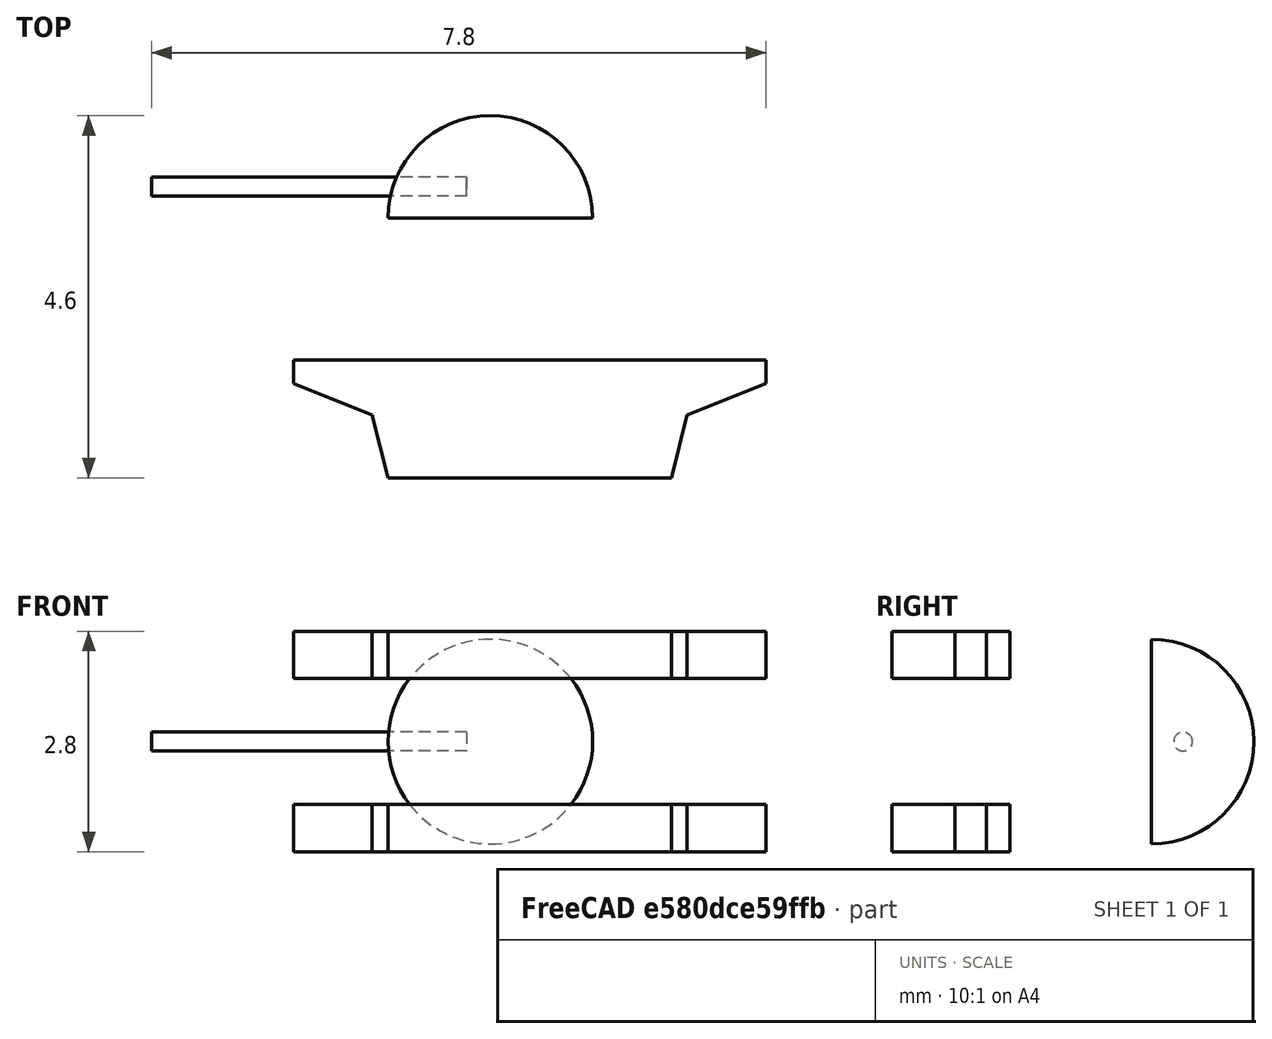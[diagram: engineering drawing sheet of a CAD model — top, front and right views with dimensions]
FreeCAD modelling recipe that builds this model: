
FCSTD DOCUMENT  (FreeCAD 0.15R4671 (Git))
Label: track
License: All rights reserved
LicenseURL: http://en.wikipedia.org/wiki/All_rights_reserved
objects: Part::Part2DObjectPython×2, Part::Extrusion×2, Mesh::Feature×1, Part::Sphere×1, Part::Cylinder×1
note: 6 computed .brp shape members not serialized (recipe doc carries the construction recipe); baked Part::Feature solids carry a one-line shape summary decoded from their .brp

FEATURE [Part::Part2DObjectPython] DWire  # Draft 2D object (typed FeaturePython)
  ChamferSize = 0
  Closed = true
  End = (3,1.2,0)
  FilletRadius = 0
  Length = 14.0033
  MakeFace = true
  Points = (8) [(3,1.5,0),(-3,1.5,0),(-3,1.2,0),(-2,0.8,0),(-1.8,0,0),(1.8,0,0),(2,0.8,0),(3,1.2,0)]
  Start = (3,1.5,0)
FEATURE [Part::Extrusion] Extrude
  Base = -> DWire
  Dir = (0,0,0.6)
  Placement = pos=(0,-1.5,-1.4) rot=(0,0,1;0rad)
  Solid = true
FEATURE [Part::Part2DObjectPython] DWire001  # Draft 2D object (typed FeaturePython)
  ChamferSize = 0
  Closed = true
  End = (3,1.2,0)
  FilletRadius = 0
  Length = 14.0033
  MakeFace = true
  Points = (8) [(3,1.5,0),(-3,1.5,0),(-3,1.2,0),(-2,0.8,0),(-1.8,0,0),(1.8,0,0),(2,0.8,0),(3,1.2,0)]
  Start = (3,1.5,0)
FEATURE [Part::Extrusion] Extrude001
  Base = -> DWire001
  Dir = (0,0,0.6)
  Placement = pos=(0,-1.5,0.8) rot=(0,0,1;0rad)
  Solid = true
FEATURE [Mesh::Feature] body
  Placement = pos=(0,0,0) rot=(-1,0,0;1.5708rad)
FEATURE [Part::Sphere] Sphere
  Angle1 = -90
  Angle2 = 90
  Angle3 = 180
  Placement = pos=(-0.5,1.8,0) rot=(0,0,1;0rad)
  Radius = 1.3
FEATURE [Part::Cylinder] Cylinder
  Angle = 360
  Height = 4
  Placement = pos=(-0.8,2.2,0) rot=(0,-1,0;1.5708rad)
  Radius = 0.12
